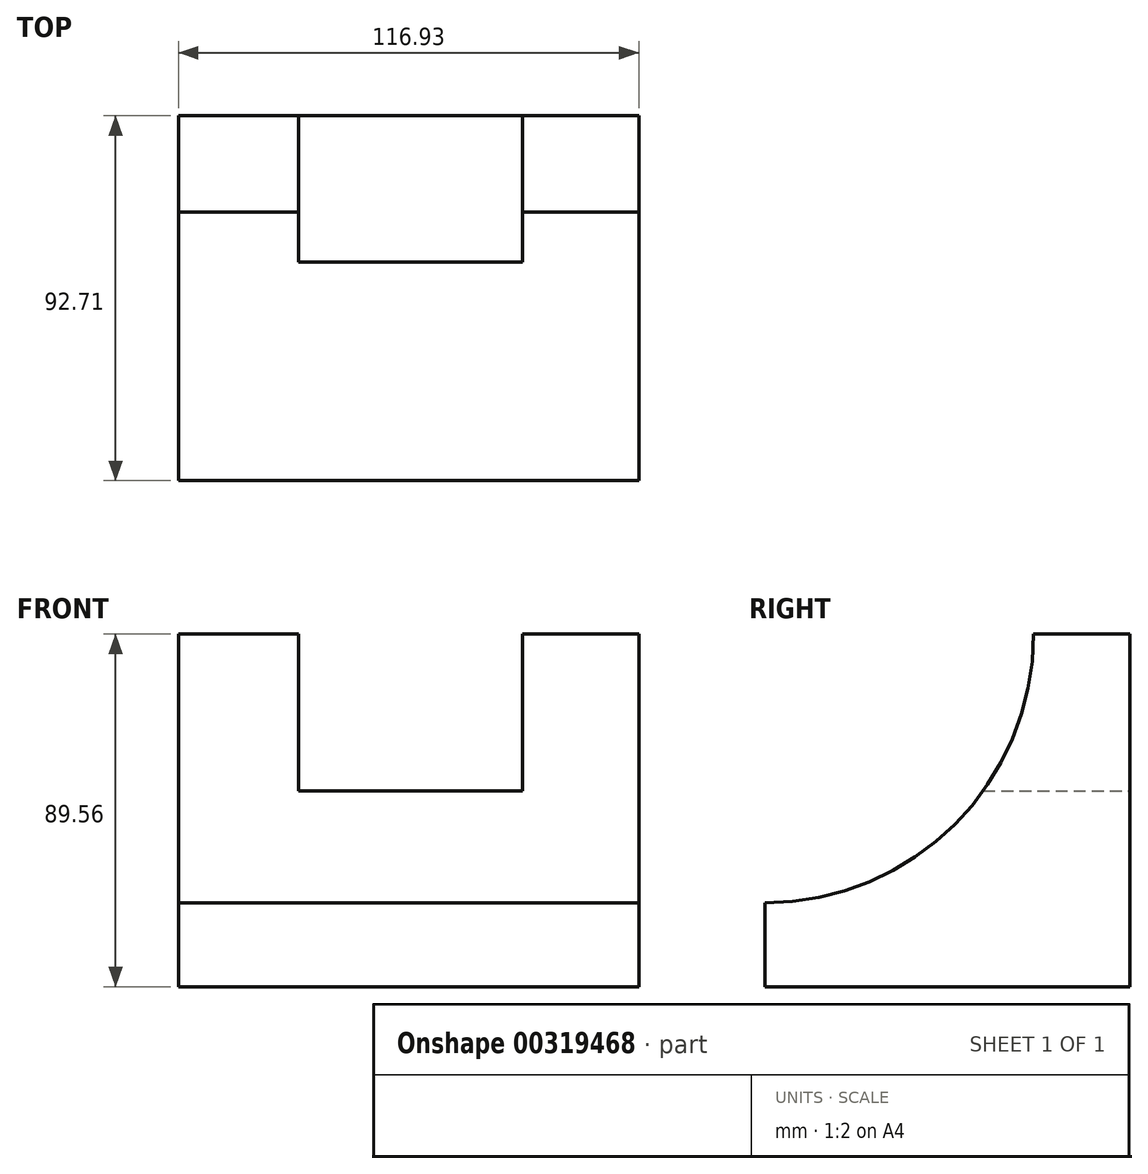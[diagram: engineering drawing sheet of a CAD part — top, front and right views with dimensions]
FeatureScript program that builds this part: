
annotation { "Feature Type Name" : "Feature", "Feature Type Description" : "" }
export const myFeature = defineFeature(function(context is Context, id is Id, definition is map)
    precondition{}
    {
        {
            var Q0;
            Q0=qCreatedBy(makeId("Front.planeOp"),FACE);
            var sketch = newSketch(context, id + "F0", { "sketchPlane" : qUnion([Q0])});
            skLineSegment(sketch, "E0.bottom", {"start": v(-43.22, 43.3) * mm, "end": v(73.7, 43.3) * mm});
            skLineSegment(sketch, "E0.top", {"start": v(-43.22, -46.26) * mm, "end": v(73.7, -46.26) * mm});
            skLineSegment(sketch, "E0.left", {"start": v(-43.22, 43.3) * mm, "end": v(-43.22, -46.26) * mm});
            skLineSegment(sketch, "E0.right", {"start": v(73.7, 43.3) * mm, "end": v(73.7, -46.26) * mm});
            skSolve(sketch);
        }
        {
            var Q0;
            Q0=makeQuery(id+"F0.imprint","IMPRINT",FACE,{"disambiguationData":[TD([[makeQuery(id+"F0.imprint","IMPRINT",EDGE,{"derivedFrom":sQuery(id+"F0.wireOp",EDGE,"E0.bottom")}),-1.0]])]});
            extrude(context, id + "F1", {"entities" : qUnion([Q0]), "depth" : 92.7 * mm, "offsetDistance" : 25.4 * mm});
        }
        {
            var Q0;
            Q0=makeQuery(id+"F1.opExtrude","SWEPT_FACE",FACE,{"disambiguationData":[OSD([sQuery(id+"F0.wireOp",EDGE,"E0.left")])]});
            var sketch = newSketch(context, id + "F2", { "sketchPlane" : qUnion([Q0])});
            skCircle(sketch, "E1", {"center": v(92.7, 43.3) * mm, "radius": 68.3 * mm});
            skSolve(sketch);
        }
        {
            var Q0;
            {var subQ0=sQuery(id+"F2.wireOp",EDGE,"E1");var subQ1=sQuery(id+"F0.wireOp",EDGE,"E0.left");var subQ4=makeQuery(id+"F1.opExtrude","CAP_EDGE",EDGE,{"disambiguationData":[OSD([subQ1])],"isStart":false});var subQ5=makeQuery(id+"F2.imprint","INTERSECT",VERTEX,{"derivedFrom":[subQ4,subQ0]});Q0=makeQuery(id+"F2.imprint","IMPRINT",FACE,{"disambiguationData":[TD([[makeQuery(id+"F2.imprint","IMPRINT",EDGE,{"disambiguationData":[TD([[subQ5,-1.0]])],"derivedFrom":subQ0}),1.0]])]});}
            var Q1;
            {var subQ0=sQuery(id+"F2.wireOp",EDGE,"E1");var subQ1=sQuery(id+"F0.wireOp",EDGE,"E0.left");var subQ4=makeQuery(id+"F1.opExtrude","CAP_EDGE",EDGE,{"disambiguationData":[OSD([subQ1])],"isStart":false});var subQ5=makeQuery(id+"F2.imprint","INTERSECT",VERTEX,{"derivedFrom":[subQ4,subQ0]});Q1=makeQuery(id+"F2.imprint","IMPRINT",FACE,{"disambiguationData":[TD([[makeQuery(id+"F2.imprint","IMPRINT",EDGE,{"disambiguationData":[TD([[subQ5,1.0]])],"derivedFrom":subQ0}),1.0]])]});}
            extrude(context, id + "F3", {"entities" : qUnion([Q0, Q1]), "operationType" : NewBodyOperationType.REMOVE, "endBound" : BoundingType.THROUGH_ALL, "oppositeDirection" : true, "depth" : 67.06 * mm, "offsetDistance" : 25.4 * mm});
        }
        {
            var Q0;
            Q0=makeQuery(id+"F1.opExtrude","CAP_FACE",FACE,{"disambiguationData":[OSD([sQuery(id+"F0.wireOp",EDGE,"E0.bottom"),sQuery(id+"F0.wireOp",EDGE,"E0.top"),sQuery(id+"F0.wireOp",EDGE,"E0.left"),sQuery(id+"F0.wireOp",EDGE,"E0.right")])],"isStart":true});
            var sketch = newSketch(context, id + "F4", { "sketchPlane" : qUnion([Q0])});
            skLineSegment(sketch, "E2.bottom", {"start": v(-44.22, 43.3) * mm, "end": v(12.73, 43.3) * mm});
            skLineSegment(sketch, "E2.top", {"start": v(-44.22, 3.5) * mm, "end": v(12.73, 3.5) * mm});
            skLineSegment(sketch, "E2.left", {"start": v(-44.22, 43.3) * mm, "end": v(-44.22, 3.5) * mm});
            skLineSegment(sketch, "E2.right", {"start": v(12.73, 43.3) * mm, "end": v(12.73, 3.5) * mm});
            skSolve(sketch);
        }
        {
            var Q0;
            Q0=makeQuery(id+"F4.imprint","IMPRINT",FACE,{"disambiguationData":[TD([[makeQuery(id+"F4.imprint","IMPRINT",EDGE,{"derivedFrom":sQuery(id+"F4.wireOp",EDGE,"E2.bottom")}),1.0]])]});
            extrude(context, id + "F5", {"entities" : qUnion([Q0]), "operationType" : NewBodyOperationType.REMOVE, "endBound" : BoundingType.THROUGH_ALL, "oppositeDirection" : true, "depth" : 25.4 * mm, "offsetDistance" : 25.4 * mm});
        }
    });
